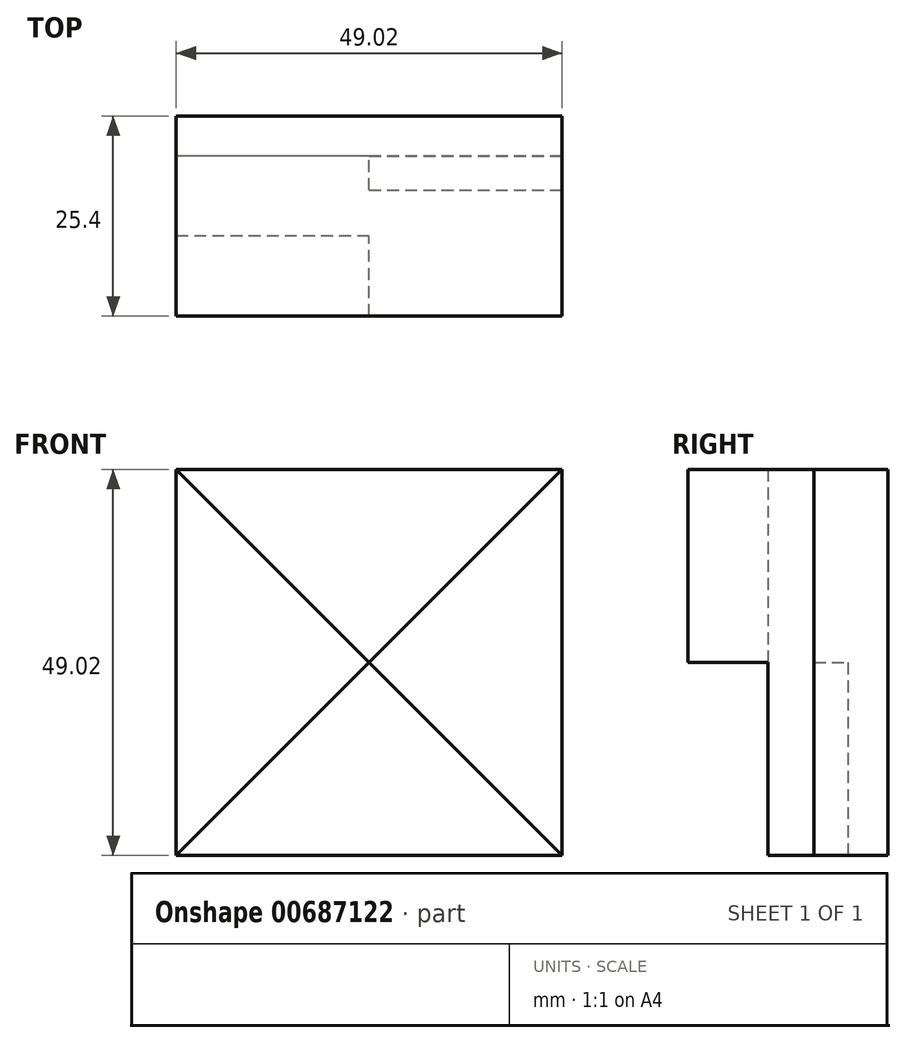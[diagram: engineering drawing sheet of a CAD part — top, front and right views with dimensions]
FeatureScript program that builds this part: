
annotation { "Feature Type Name" : "Feature", "Feature Type Description" : "" }
export const myFeature = defineFeature(function(context is Context, id is Id, definition is map)
    precondition{}
    {
        {
            var Q0;
            Q0=qCreatedBy(makeId("Front.planeOp"),FACE);
            var sketch = newSketch(context, id + "F0", { "sketchPlane" : qUnion([Q0])});
            skLineSegment(sketch, "E0.bottom", {"start": v(24.51, -24.51) * mm, "end": v(-24.51, -24.51) * mm});
            skLineSegment(sketch, "E0.top", {"start": v(24.51, 24.51) * mm, "end": v(-24.51, 24.51) * mm});
            skLineSegment(sketch, "E0.left", {"start": v(24.51, -24.51) * mm, "end": v(24.51, 24.51) * mm});
            skLineSegment(sketch, "E0.right", {"start": v(-24.51, -24.51) * mm, "end": v(-24.51, 24.51) * mm});
            skPoint(sketch, "E0.middle", {"position": v(0, 0) * mm});
            skLineSegment(sketch, "E1", {"start": v(-24.51, 24.51) * mm, "end": v(0, 0) * mm});
            skLineSegment(sketch, "E2", {"start": v(0, 0) * mm, "end": v(24.51, 24.51) * mm});
            skLineSegment(sketch, "E3", {"start": v(0, 0) * mm, "end": v(-24.51, -24.51) * mm});
            skLineSegment(sketch, "E4", {"start": v(0, 0) * mm, "end": v(24.51, -24.51) * mm});
            skSolve(sketch);
        }
        {
            var Q0;
            Q0=makeQuery(id+"F0.imprint","IMPRINT",FACE,{"disambiguationData":[TD([[makeQuery(id+"F0.imprint","IMPRINT",EDGE,{"derivedFrom":sQuery(id+"F0.wireOp",EDGE,"E0.top")}),1.0]])]});
            extrude(context, id + "F1", {"entities" : qUnion([Q0]), "depth" : 25.4 * mm, "offsetDistance" : 25.4 * mm});
        }
        {
            var Q0;
            Q0=makeQuery(id+"F0.imprint","IMPRINT",FACE,{"disambiguationData":[TD([[makeQuery(id+"F0.imprint","IMPRINT",EDGE,{"derivedFrom":sQuery(id+"F0.wireOp",EDGE,"E0.right")}),-1.0]])]});
            extrude(context, id + "F2", {"entities" : qUnion([Q0]), "operationType" : NewBodyOperationType.ADD, "depth" : 15.24 * mm, "offsetDistance" : 25.4 * mm});
        }
        {
            var Q0;
            Q0=makeQuery(id+"F0.imprint","IMPRINT",FACE,{"disambiguationData":[TD([[makeQuery(id+"F0.imprint","IMPRINT",EDGE,{"derivedFrom":sQuery(id+"F0.wireOp",EDGE,"E0.left")}),1.0]])]});
            extrude(context, id + "F3", {"entities" : qUnion([Q0]), "operationType" : NewBodyOperationType.ADD, "depth" : 9.4 * mm, "offsetDistance" : 25.4 * mm});
        }
        {
            var Q0;
            Q0=makeQuery(id+"F0.imprint","IMPRINT",FACE,{"disambiguationData":[TD([[makeQuery(id+"F0.imprint","IMPRINT",EDGE,{"derivedFrom":sQuery(id+"F0.wireOp",EDGE,"E0.bottom")}),-1.0]])]});
            extrude(context, id + "F4", {"entities" : qUnion([Q0]), "operationType" : NewBodyOperationType.ADD, "depth" : 5.08 * mm, "offsetDistance" : 25.4 * mm});
        }
    });
